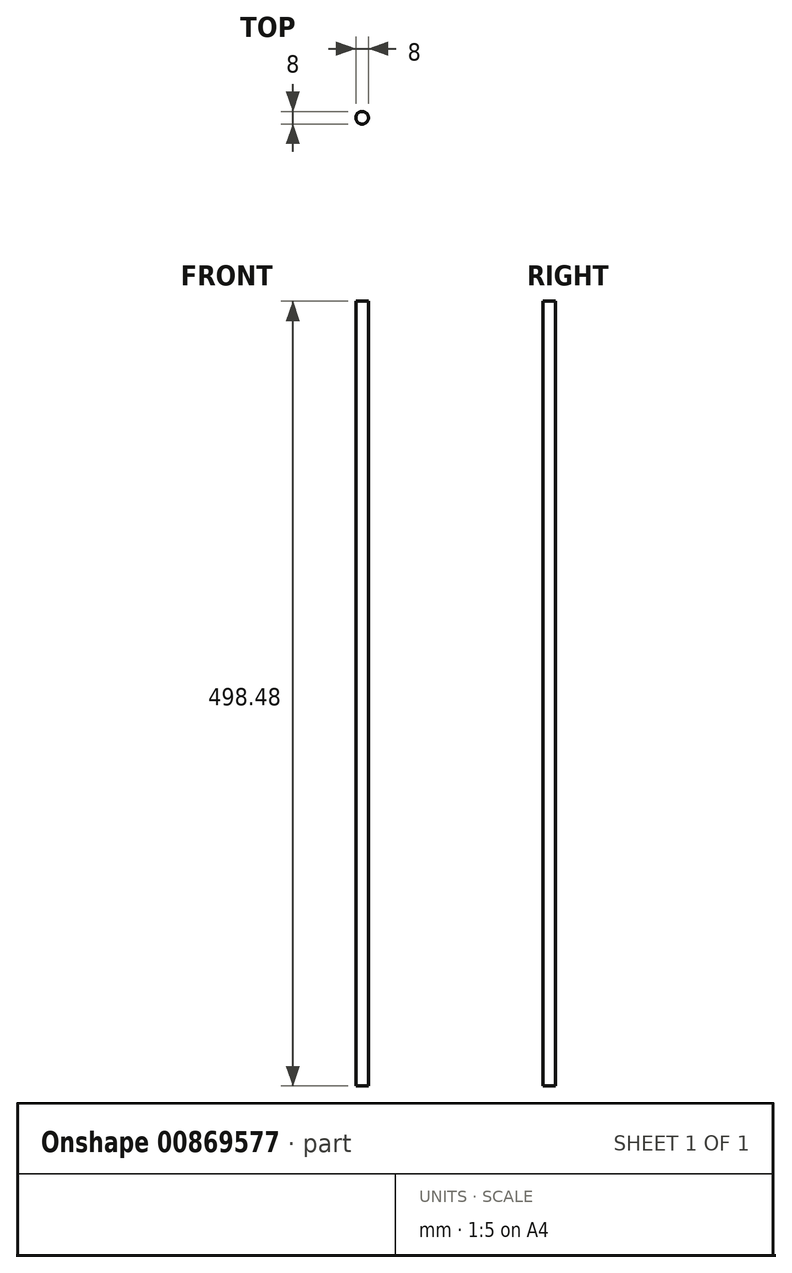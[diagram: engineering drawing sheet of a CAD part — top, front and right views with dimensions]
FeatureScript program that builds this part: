
annotation { "Feature Type Name" : "Feature", "Feature Type Description" : "" }
export const myFeature = defineFeature(function(context is Context, id is Id, definition is map)
    precondition{}
    {
        {
            var Q0;
            Q0=qCreatedBy(makeId("Top.planeOp"),FACE);
            var sketch = newSketch(context, id + "F0", { "sketchPlane" : qUnion([Q0])});
            skCircle(sketch, "E0", {"center": v(0, 0) * mm, "radius": 4 * mm});
            skSolve(sketch);
        }
        {
            var Q0;
            Q0 = qSketchRegion(id + "F0", true);
            extrude(context, id + "F1", {"entities" : qUnion([Q0]), "flatOperationType" : FlatOperationType.REMOVE, "depth" : 498.47 * mm, "offsetDistance" : 25.4 * mm, "domain" : OperationDomain.MODEL});
        }
    });
